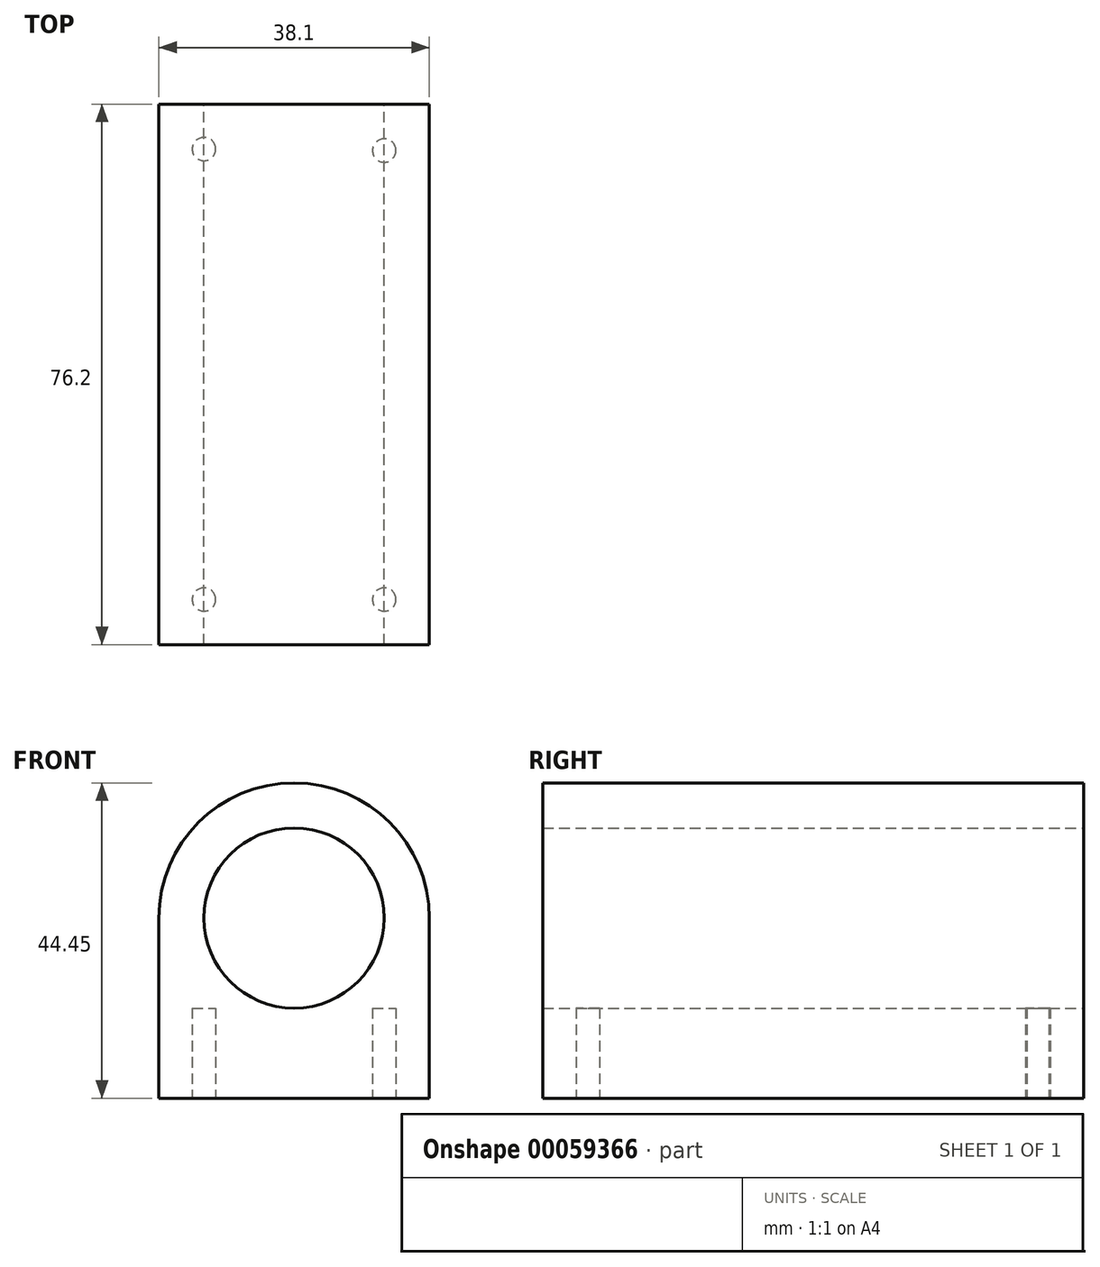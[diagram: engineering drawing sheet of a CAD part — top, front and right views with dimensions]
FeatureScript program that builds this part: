
annotation { "Feature Type Name" : "Feature", "Feature Type Description" : "" }
export const myFeature = defineFeature(function(context is Context, id is Id, definition is map)
    precondition{}
    {
        {
            var Q0;
            Q0=qCreatedBy(makeId("Front.planeOp"),FACE);
            var sketch = newSketch(context, id + "F0", { "sketchPlane" : qUnion([Q0])});
            skCircle(sketch, "E0", {"center": v(0, 0) * mm, "radius": 12.7 * mm});
            skArc(sketch, "E1", {"start": v(19.05, 0) * mm, "mid": v(0, 19.05) * mm, "end": v(-19.05, 0) * mm});
            skLineSegment(sketch, "E2", {"start": v(-19.05, 0) * mm, "end": v(-19.05, -25.4) * mm});
            skLineSegment(sketch, "E3", {"start": v(-19.05, -25.4) * mm, "end": v(19.05, -25.4) * mm});
            skLineSegment(sketch, "E4", {"start": v(19.05, -25.4) * mm, "end": v(19.05, 0) * mm});
            skSolve(sketch);
        }
        {
            var Q0;
            Q0=makeQuery(id+"F0.imprint","IMPRINT",FACE,{"disambiguationData":[TD([[makeQuery(id+"F0.imprint","IMPRINT",EDGE,{"derivedFrom":sQuery(id+"F0.wireOp",EDGE,"E0")}),-1.0]])]});
            extrude(context, id + "F1", {"entities" : qUnion([Q0]), "depth" : 76.2 * mm});
        }
        {
            var Q0;
            Q0=makeQuery(id+"F1.opExtrude","SWEPT_FACE",FACE,{"disambiguationData":[OSD([sQuery(id+"F0.wireOp",EDGE,"E3")])]});
            var sketch = newSketch(context, id + "F2", { "sketchPlane" : qUnion([Q0])});
            skCircle(sketch, "E5", {"center": v(-12.7, 69.85) * mm, "radius": 1.65 * mm});
            skCircle(sketch, "E6", {"center": v(12.7, 69.85) * mm, "radius": 1.65 * mm});
            skCircle(sketch, "E7", {"center": v(-12.7, 6.35) * mm, "radius": 1.65 * mm});
            skCircle(sketch, "E8", {"center": v(12.7, 6.55) * mm, "radius": 1.65 * mm});
            skSolve(sketch);
        }
        {
            var Q0;
            Q0 = qSketchRegion(id + "F2", true);
            extrude(context, id + "F3", {"entities" : qUnion([Q0]), "operationType" : NewBodyOperationType.REMOVE, "oppositeDirection" : true, "depth" : 12.7 * mm});
        }
    });
